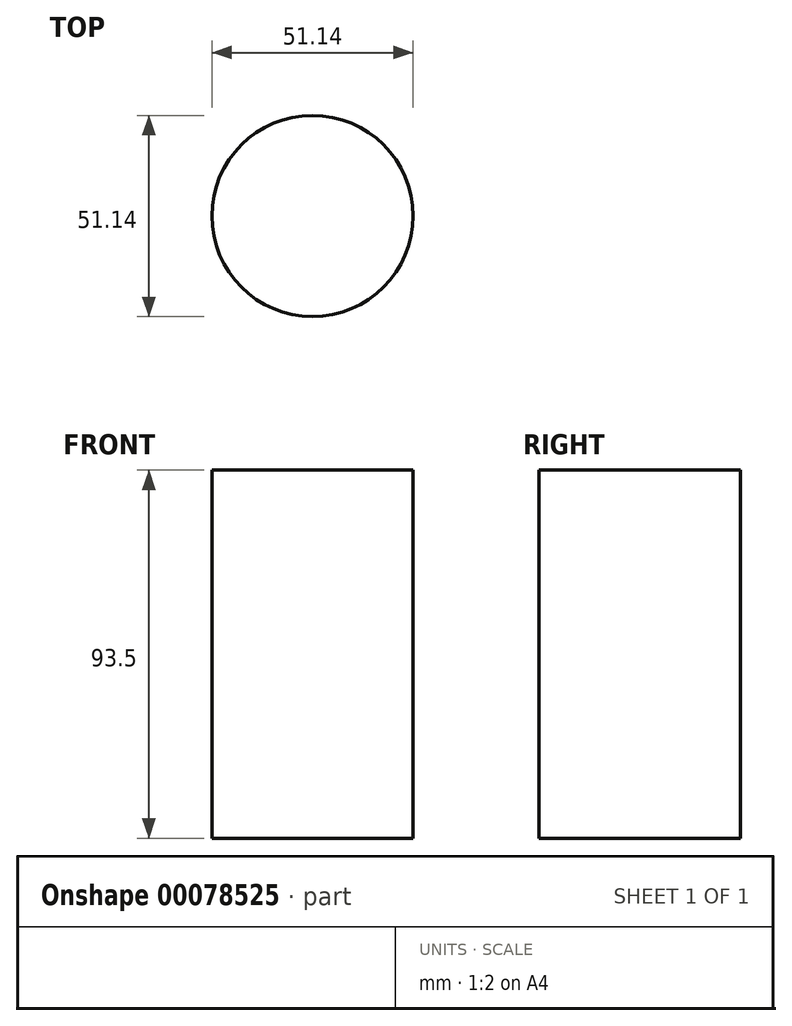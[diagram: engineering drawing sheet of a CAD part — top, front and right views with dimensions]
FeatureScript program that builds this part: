
annotation { "Feature Type Name" : "Feature", "Feature Type Description" : "" }
export const myFeature = defineFeature(function(context is Context, id is Id, definition is map)
    precondition{}
    {
        {
            var Q0;
            Q0=qCreatedBy(makeId("Right.planeOp"),FACE);
            var sketch = newSketch(context, id + "F0", { "sketchPlane" : qUnion([Q0])});
            skLineSegment(sketch, "E0.bottom", {"start": v(0, 93.5) * mm, "end": v(25.57, 93.5) * mm});
            skLineSegment(sketch, "E0.top", {"start": v(0, 0) * mm, "end": v(25.57, 0) * mm});
            skLineSegment(sketch, "E0.left", {"start": v(0, 93.5) * mm, "end": v(0, 0) * mm});
            skLineSegment(sketch, "E0.right", {"start": v(25.57, 93.5) * mm, "end": v(25.57, 0) * mm});
            skLineSegment(sketch, "E1", {"start": v(0, -28.35) * mm, "end": v(0, 119.7) * mm, "construction": true});
            skSolve(sketch);
        }
        {
            var Q0;
            Q0=makeQuery(id+"F0.imprint","IMPRINT",FACE,{"disambiguationData":[TD([[makeQuery(id+"F0.imprint","IMPRINT",EDGE,{"derivedFrom":sQuery(id+"F0.wireOp",EDGE,"E0.bottom")}),-1.0]])]});
            var Q1;
            Q1=sQuery(id+"F0.wireOp",EDGE,"E1");
            var Q2;
            Q2=sQuery(id+"F0.wireOp",EDGE,"E0.right");
            var Q3;
            Q3=sQuery(id+"F0.wireOp",EDGE,"E1");
            revolve(context, id + "F1", {"entities" : qUnion([Q0]), "surfaceEntities" : qUnion([Q1, Q2]), "axis" : qUnion([Q3]), "revolveType" : RevolveType.FULL});
        }
    });
